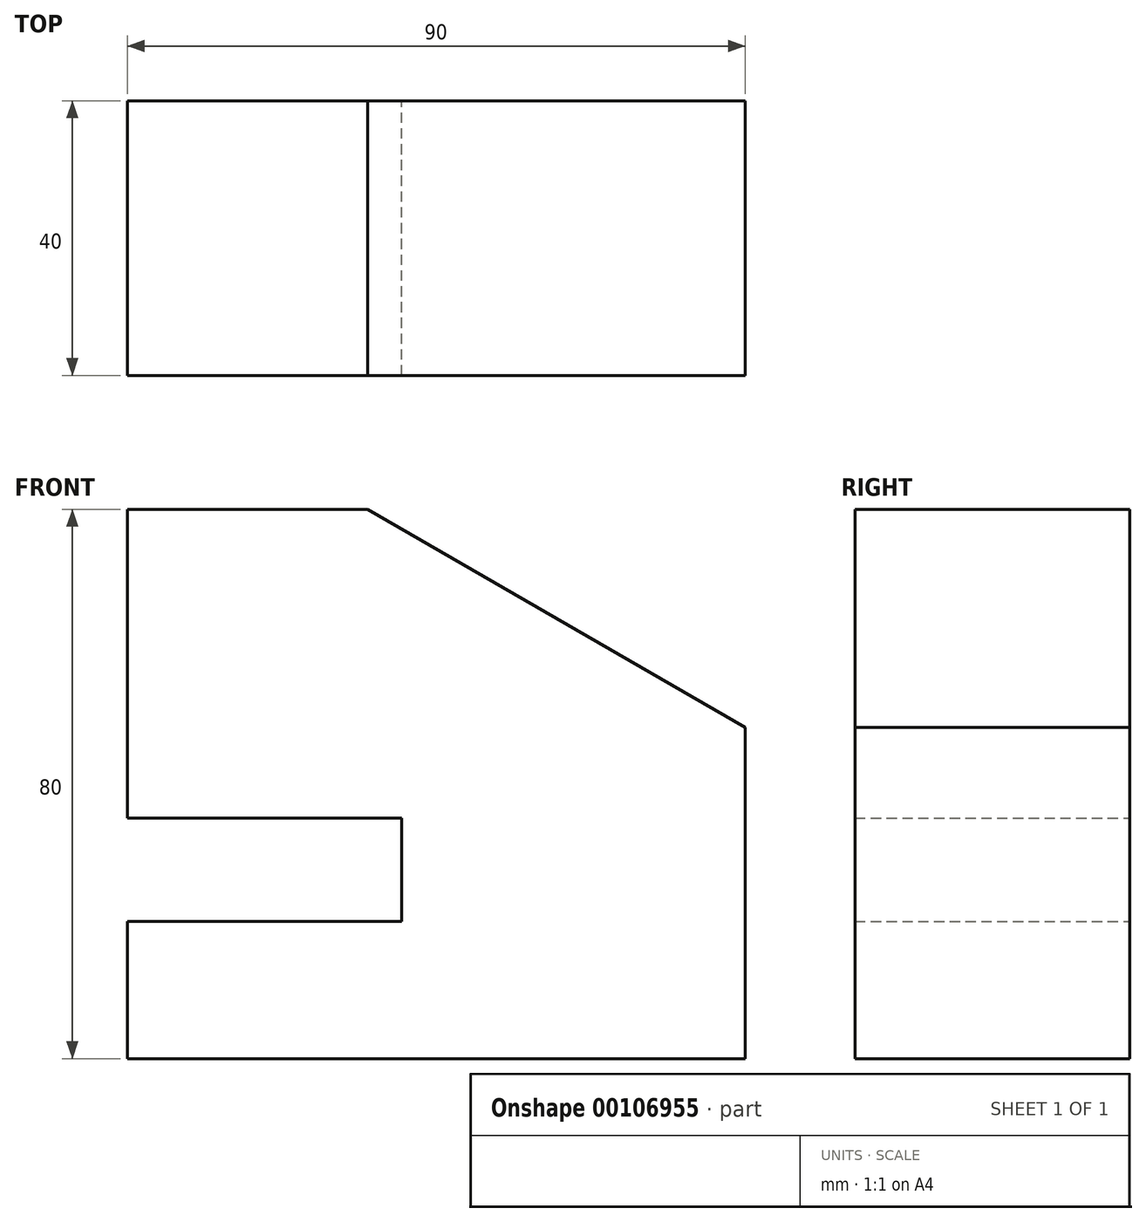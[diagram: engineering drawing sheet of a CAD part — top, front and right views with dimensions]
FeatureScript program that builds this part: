
annotation { "Feature Type Name" : "Feature", "Feature Type Description" : "" }
export const myFeature = defineFeature(function(context is Context, id is Id, definition is map)
    precondition{}
    {
        {
            var Q0;
            Q0=qCreatedBy(makeId("Front.planeOp"),FACE);
            var sketch = newSketch(context, id + "F0", { "sketchPlane" : qUnion([Q0])});
            skLineSegment(sketch, "E0", {"start": v(0, 0) * mm, "end": v(0, 20) * mm});
            skLineSegment(sketch, "E1", {"start": v(0, 20) * mm, "end": v(40, 20) * mm});
            skLineSegment(sketch, "E2", {"start": v(40, 20) * mm, "end": v(40, 35) * mm});
            skLineSegment(sketch, "E3", {"start": v(40, 35) * mm, "end": v(0, 35) * mm});
            skLineSegment(sketch, "E4", {"start": v(0, 35) * mm, "end": v(0, 80) * mm});
            skLineSegment(sketch, "E5", {"start": v(0, 80) * mm, "end": v(35, 80) * mm});
            skLineSegment(sketch, "E6", {"start": v(35, 80) * mm, "end": v(90, 48.25) * mm});
            skLineSegment(sketch, "E7", {"start": v(90, 48.25) * mm, "end": v(90, 0) * mm});
            skLineSegment(sketch, "E8", {"start": v(90, 0) * mm, "end": v(0, 0) * mm});
            skSolve(sketch);
        }
        {
            var Q0;
            Q0=qSketchRegion(id+"F0",true);
            extrude(context, id + "F1", {"entities" : qUnion([Q0]), "endBound" : BoundingType.SYMMETRIC, "depth" : 40 * mm});
        }
    });
